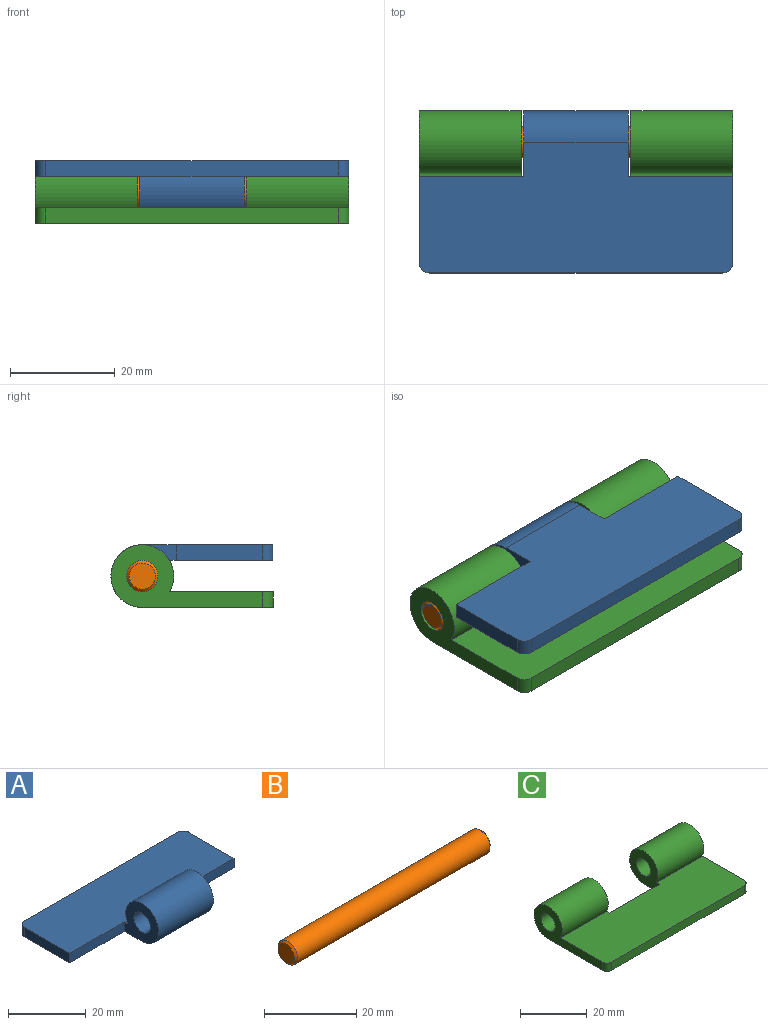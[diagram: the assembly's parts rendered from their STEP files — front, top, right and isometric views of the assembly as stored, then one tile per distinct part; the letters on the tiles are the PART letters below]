
ASSEMBLY  parts=3 mates=2
PART A: 13 faces, bbox 60x31x12 mm
  f0: plane 20x3mm, normal (0,-1,0), area 60mm2, adj f1,f2,f4,f8
  f1: plane 12.5x12mm, normal (-1,0,0), area 93.3mm2, adj f0,f2,f5,f7,f8
  f2: plane 60x25mm, normal (0,0,-1), area 1238.3mm2, adj f0,f1,f3,f4,f6,f7,f9,f10
  f3: plane 16.5x3mm, normal (1,0,0), area 49.5mm2, adj f2,f8,f9,f10
  f4: plane 16.5x3mm, normal (-1,0,0), area 49.5mm2, adj f0,f2,f8,f12
  f5: cylinder r=3mm len=20mm, axis (1,0,0), area 377mm2, adj f1,f11
  f6: plane 56x3mm, normal (0,1,0), area 168mm2, adj f2,f8,f9,f12
  f7: cylinder r=6mm len=20mm, axis (1,0,0), area 628.3mm2, adj f1,f2,f8,f11
  f8: plane 60x19.8mm, normal (0,0,1), area 1134.4mm2, adj f0,f1,f3,f4,f6,f7,f9,f10
  f9: cylinder r=2mm len=3mm, axis (0,0,1), area 9.4mm2, adj f2,f3,f6,f8
  f10: plane 20x3mm, normal (0,-1,0), area 60mm2, adj f2,f3,f8,f11
  f11: plane 12.5x12mm, normal (1,0,0), area 93.3mm2, adj f2,f5,f7,f8,f10
  f12: cylinder r=2mm len=3mm, axis (0,0,1), area 9.4mm2, adj f2,f4,f6,f8
PART B: 5 faces, bbox 60x6x6 mm
  f0: cone r=3mm half-angle=45deg, axis (-1,0,0), area 12.2mm2, adj f1,f4
  f1: cylinder r=3mm len=59mm, axis (-1,0,0), area 1112.1mm2, adj f0,f2
  f2: cone r=2.5mm half-angle=45deg, axis (1,0,0), area 12.2mm2, adj f1,f3
  f3: plane 5x5mm, normal (-1,0,0), area 19.6mm2, adj f2
  f4: plane 5x5mm, normal (1,0,0), area 19.6mm2, adj f0
PART C: 14 faces, bbox 60x31x12 mm
  f0: cylinder r=6mm len=19.5mm, axis (1,0,0), area 612.6mm2, adj f3,f4,f7,f9
  f1: cylinder r=6mm len=19.5mm, axis (1,0,0), area 612.6mm2, adj f3,f4,f8,f11
  f2: cylinder r=3mm len=19.5mm, axis (1,0,0), area 367.6mm2, adj f8,f11
  f3: plane 60x19.8mm, normal (0,0,1), area 1159.1mm2, adj f0,f1,f5,f7,f8,f9,f10,f11
  f4: plane 60x25mm, normal (0,0,-1), area 1361.8mm2, adj f0,f1,f5,f7,f8,f9,f10,f11
  f5: plane 56x3mm, normal (0,-1,0), area 168mm2, adj f3,f4,f12,f13
  f6: cylinder r=3mm len=19.5mm, axis (1,0,0), area 367.6mm2, adj f7,f9
  f7: plane 29x12mm, normal (-1,0,0), area 142.8mm2, adj f0,f3,f4,f6,f13
  f8: plane 29x12mm, normal (1,0,0), area 142.8mm2, adj f1,f2,f3,f4,f12
  f9: plane 12.5x12mm, normal (1,0,0), area 93.3mm2, adj f0,f3,f4,f6,f10
  f10: plane 21x3mm, normal (0,1,0), area 63mm2, adj f3,f4,f9,f11
  f11: plane 12.5x12mm, normal (-1,0,0), area 93.3mm2, adj f1,f2,f3,f4,f10
  f12: cylinder r=2mm len=3mm, axis (0,0,-1), area 9.4mm2, adj f3,f4,f5,f8
  f13: cylinder r=2mm len=3mm, axis (0,0,-1), area 9.4mm2, adj f3,f4,f5,f7
PLACE A rot(axis=(1,0,0),179.9deg) t=(-10.41,36.45,-46.02)mm
PLACE B t=(-10.41,36.45,-46.02)mm
PLACE C t=(-10.41,36.45,-46.02)mm
MATE fastened B.f0 <-> C.f2  axis (1,0,0) through (19.59,36.45,-46.02)mm
MATE revolute B.f0 <-> A.f7  axis (-1,0,0) through (-10.41,36.45,-46.02)mm
